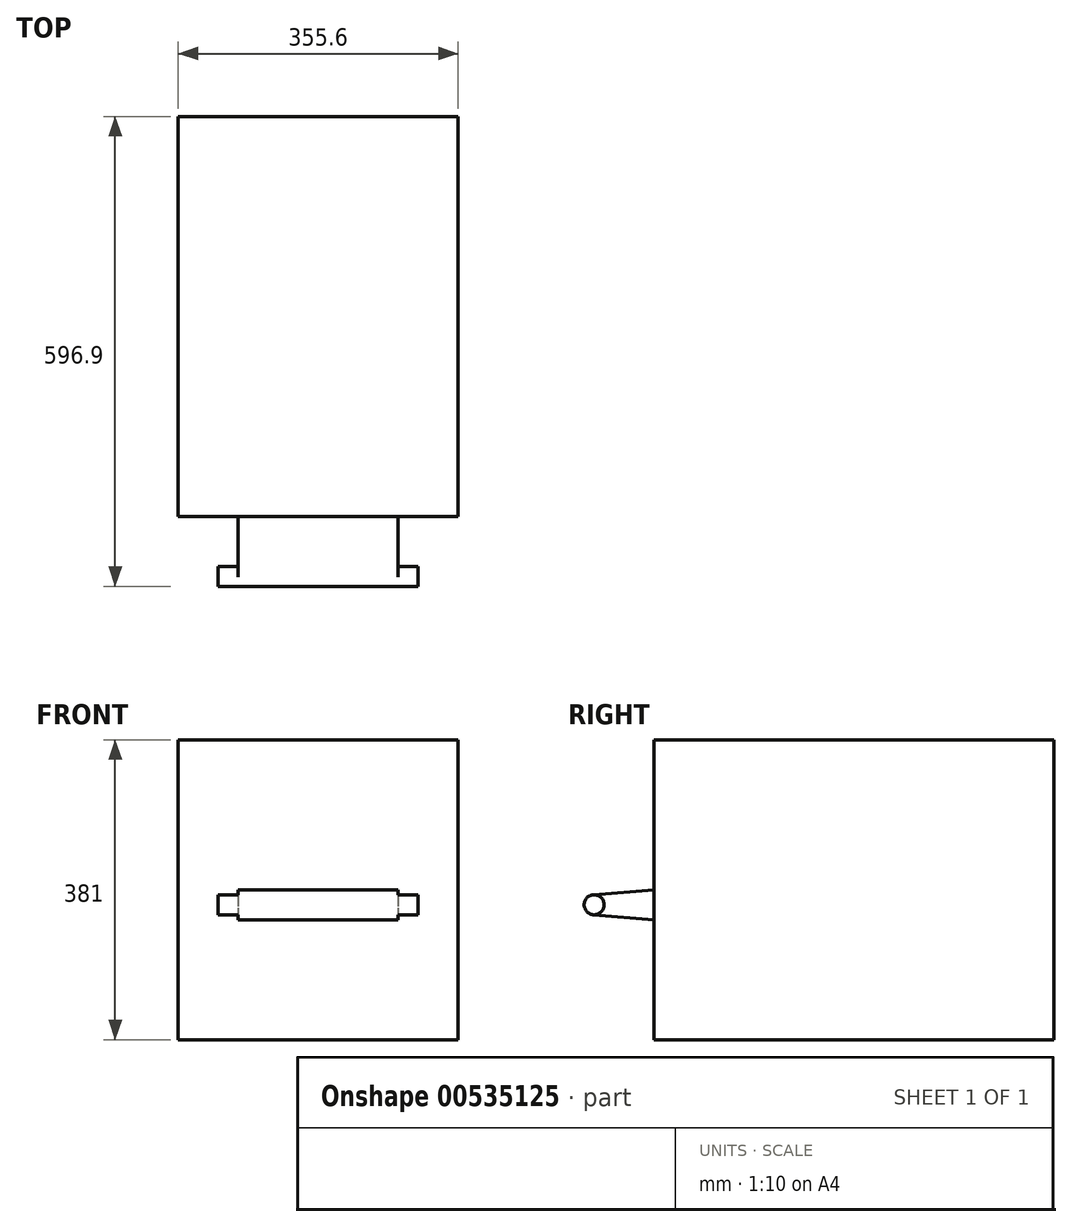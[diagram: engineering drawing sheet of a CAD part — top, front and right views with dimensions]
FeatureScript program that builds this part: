
annotation { "Feature Type Name" : "Feature", "Feature Type Description" : "" }
export const myFeature = defineFeature(function(context is Context, id is Id, definition is map)
    precondition{}
    {
        {
            var Q0;
            Q0=qCreatedBy(makeId("Top.planeOp"),FACE);
            var sketch = newSketch(context, id + "F0", { "sketchPlane" : qUnion([Q0])});
            skLineSegment(sketch, "E0.bottom", {"start": v(0, 0) * mm, "end": v(355.6, 0) * mm});
            skLineSegment(sketch, "E0.top", {"start": v(0, 508) * mm, "end": v(355.6, 508) * mm});
            skLineSegment(sketch, "E0.left", {"start": v(0, 0) * mm, "end": v(0, 508) * mm});
            skLineSegment(sketch, "E0.right", {"start": v(355.6, 0) * mm, "end": v(355.6, 508) * mm});
            skSolve(sketch);
        }
        {
            var Q0;
            Q0=qSketchRegion(id+"F0",true);
            extrude(context, id + "F1", {"entities" : qUnion([Q0]), "depth" : 381 * mm});
        }
        {
            var Q0;
            Q0=makeQuery(id+"F1.opExtrude","SWEPT_FACE",FACE,{"disambiguationData":[OSD([sQuery(id+"F0.wireOp",EDGE,"E0.left")])]});
            var Q1;
            Q1=makeQuery(id+"F1.opExtrude","SWEPT_FACE",FACE,{"disambiguationData":[OSD([sQuery(id+"F0.wireOp",EDGE,"E0.right")])]});
            cPlane(context, id + "F2", {"entities" : qUnion([Q0, Q1]), "cplaneType" : CPlaneType.MID_PLANE, "offset" : 25.4 * mm, "width" : 152.4 * mm, "height" : 152.4 * mm});
        }
        {
            var Q0;
            Q0=qCreatedBy(id+"F2.planeOp",FACE);
            var sketch = newSketch(context, id + "F3", { "sketchPlane" : qUnion([Q0])});
            skCircle(sketch, "E1", {"center": v(76.2, 171.45) * mm, "radius": 12.7 * mm});
            skLineSegment(sketch, "E2", {"start": v(0, 190.5) * mm, "end": v(77.25, 184.1) * mm});
            skLineSegment(sketch, "E3", {"start": v(0, 152.4) * mm, "end": v(77.25, 158.8) * mm});
            skLineSegment(sketch, "E4", {"start": v(0, 190.5) * mm, "end": v(0, 152.4) * mm});
            skSolve(sketch);
        }
        {
            var Q0;
            {var subQ0=sQuery(id+"F3.wireOp",EDGE,"E2");Q0=makeQuery(id+"F3.imprint","IMPRINT",FACE,{"disambiguationData":[TD([[makeQuery(id+"F3.imprint","IMPRINT",EDGE,{"derivedFrom":subQ0}),-1.0]])]});}
            var Q1;
            Q1=makeQuery(id+"F1.opExtrude","SWEPT_FACE",FACE,{"disambiguationData":[OSD([sQuery(id+"F0.wireOp",EDGE,"E0.left")])]});
            var Q2;
            Q2=makeQuery(id+"F1.opExtrude","SWEPT_FACE",FACE,{"disambiguationData":[OSD([sQuery(id+"F0.wireOp",EDGE,"E0.right")])]});
            extrude(context, id + "F4", {"entities" : qUnion([Q0]), "operationType" : NewBodyOperationType.ADD, "endBoundEntityFace" : qUnion([Q1]), "depth" : 101.6 * mm, "hasSecondDirection" : true, "secondDirectionOppositeDirection" : true, "secondDirectionBoundEntityFace" : qUnion([Q2]), "secondDirectionDepth" : 101.6 * mm});
        }
        {
            var Q0;
            {var subQ0=sQuery(id+"F3.wireOp",EDGE,"E1");var subQ1=makeQuery(id+"F3.imprint","INTERSECT",VERTEX,{"derivedFrom":[subQ0,sQuery(id+"F3.wireOp",EDGE,"E2")]});Q0=makeQuery(id+"F3.imprint","IMPRINT",FACE,{"disambiguationData":[TD([[makeQuery(id+"F3.imprint","IMPRINT",EDGE,{"disambiguationData":[TD([[subQ1,-1.0]])],"derivedFrom":subQ0}),1.0]])]});}
            var Q1;
            Q1=makeQuery(id+"F1.opExtrude","SWEPT_FACE",FACE,{"disambiguationData":[OSD([sQuery(id+"F0.wireOp",EDGE,"E0.left")])]});
            var Q2;
            Q2=makeQuery(id+"F1.opExtrude","SWEPT_FACE",FACE,{"disambiguationData":[OSD([sQuery(id+"F0.wireOp",EDGE,"E0.right")])]});
            extrude(context, id + "F5", {"entities" : qUnion([Q0]), "operationType" : NewBodyOperationType.ADD, "endBoundEntityFace" : qUnion([Q1]), "depth" : 127 * mm, "hasSecondDirection" : true, "secondDirectionOppositeDirection" : true, "secondDirectionBoundEntityFace" : qUnion([Q2]), "secondDirectionDepth" : 127 * mm});
        }
    });
